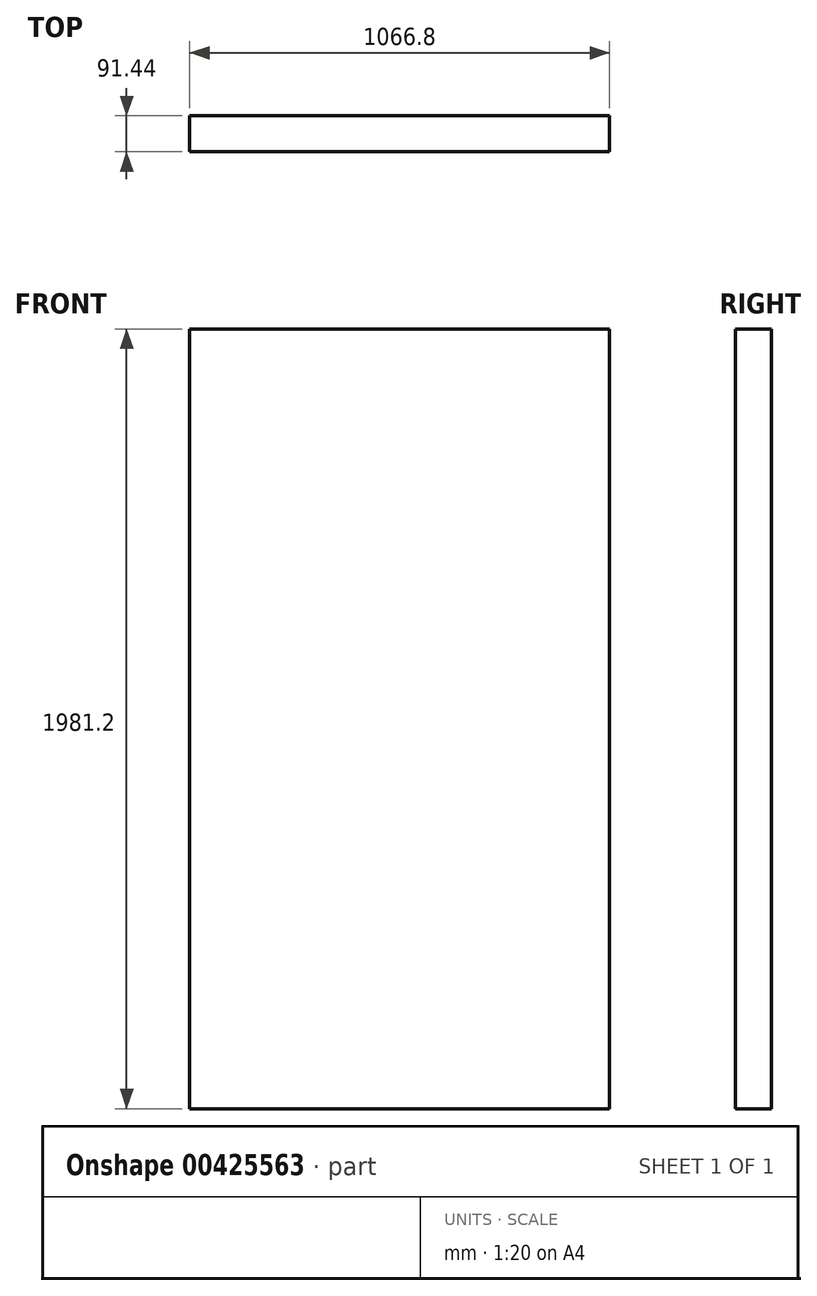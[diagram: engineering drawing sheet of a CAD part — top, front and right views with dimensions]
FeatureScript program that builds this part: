
annotation { "Feature Type Name" : "Feature", "Feature Type Description" : "" }
export const myFeature = defineFeature(function(context is Context, id is Id, definition is map)
    precondition{}
    {
        {
            var Q0;
            Q0=qCreatedBy(makeId("Front.planeOp"),FACE);
            var sketch = newSketch(context, id + "F0", { "sketchPlane" : qUnion([Q0])});
            skLineSegment(sketch, "E0.bottom", {"start": v(0, 0) * mm, "end": v(1066.8, 0) * mm});
            skLineSegment(sketch, "E0.top", {"start": v(0, 1981.2) * mm, "end": v(1066.8, 1981.2) * mm});
            skLineSegment(sketch, "E0.left", {"start": v(0, 0) * mm, "end": v(0, 1981.2) * mm});
            skLineSegment(sketch, "E0.right", {"start": v(1066.8, 0) * mm, "end": v(1066.8, 1981.2) * mm});
            skSolve(sketch);
        }
        {
            var Q0;
            Q0 = qSketchRegion(id + "F0", true);
            extrude(context, id + "F1", {"entities" : qUnion([Q0]), "depth" : 91.44 * mm});
        }
    });
